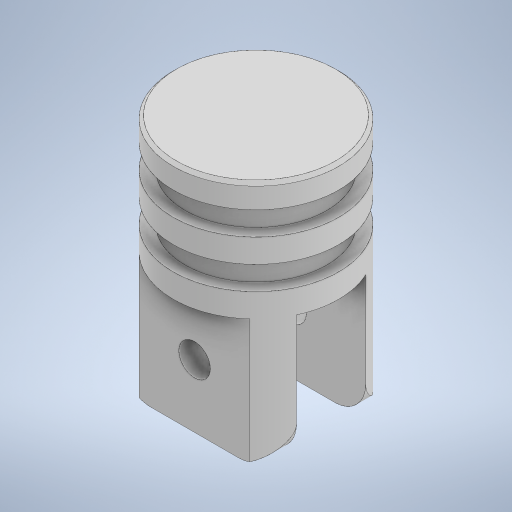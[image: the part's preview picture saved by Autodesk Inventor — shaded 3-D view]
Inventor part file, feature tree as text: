
AUTODESK INVENTOR PART (.ipt)
format: ipt  version: 2023 (Build 270158000, 158)  size: 310,272 bytes
history: native  units: in
note: dims shown in document units (in); Inventor stores cm internally (conversion verified against a paired STEP export)
features: sketch x3, extrude x2, revolve x1, chamfer x1
ambient origin geometry x8: Origin, YZ Plane, XZ Plane, XY Plane, X Axis, Y Axis, Z Axis, Center Point
bodies: Body1 (feature_tree)
feature tree (7):
  revolve  "Revolution1"  [1 undecoded]
  chamfer  "Chamfer1"  Distance=0.1875in
  extrude  "Extrusion4"  TaperAngle=360.0deg  [1 undecoded]
  extrude  "Extrusion5"  Depth=0.125in TaperAngle=45.0deg
  sketch  "Sketch5"  dims[d15=0.0938in d16=0.1875in]
  sketch  "Sketch10"  dims[d17=0.1875in]
  sketch  "Sketch11"  dims[d18=0.1875in d19=0.1875in d20=360.0deg d24=0.025in d25=0.125in d26=45.0deg d38=0.188in d52=1.0in d53=0.0in d55=0.25in d56=1.0in d57=0.0in d58=0.25in d45=0.5in d46=0.0344in d47=0.5in d48=0.0344in]
note: 2 required parameter values undecoded (feature->parameter linkage not recoverable at this tier; creation-order binding heuristic only, values carry confidence <= 0.55)